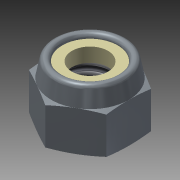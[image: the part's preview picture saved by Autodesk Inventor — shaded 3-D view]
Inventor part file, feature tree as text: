
AUTODESK INVENTOR PART (.ipt)
format: ipt  version: 2014 (Build 180170000, 170)  size: 192,000 bytes
history: native  units: mm (DEFAULTED — no unit token found)
features: sketch x5, extrude x2, revolve x2, other x1, plane x1, thread x1
ambient origin geometry x8: Origin, YZ Plane, XZ Plane, XY Plane, X Axis, Y Axis, Z Axis, Center Point
bodies: Solid1 (feature_tree)
feature tree (12):
  other  "Hexagon_flats_join1"
  extrude  "Extrusion1"  Depth=25.4mm TaperAngle=0.0deg
  revolve  "Revolution1"  Angle=90.0deg
  plane  "Work Plane1"
  extrude  "Extrusion2"  Depth=1.5875mm
  revolve  "Revolution2"  Angle=15.0deg
  thread  "Thread1"  [1 undecoded]
  sketch  "Sketch1"  dims[d0=11.1125mm d3=25.4mm d4=0.0mm]
  sketch  "Sketch2"  dims[d5=13.788101mm d7=90.0deg]
  sketch  "Sketch3"  dims[d9=25.4mm d10=0.0mm d11=1.5875mm]
  sketch  "Sketch4"  dims[d12=15.0deg d13=15.0deg d14=11.1125mm]
  sketch  "Sketch5"  dims[d15=90.0deg d16=25.4mm d17=0.0mm]
note: 1 required parameter value undecoded (feature->parameter linkage not recoverable at this tier; creation-order binding heuristic only, values carry confidence <= 0.55)
